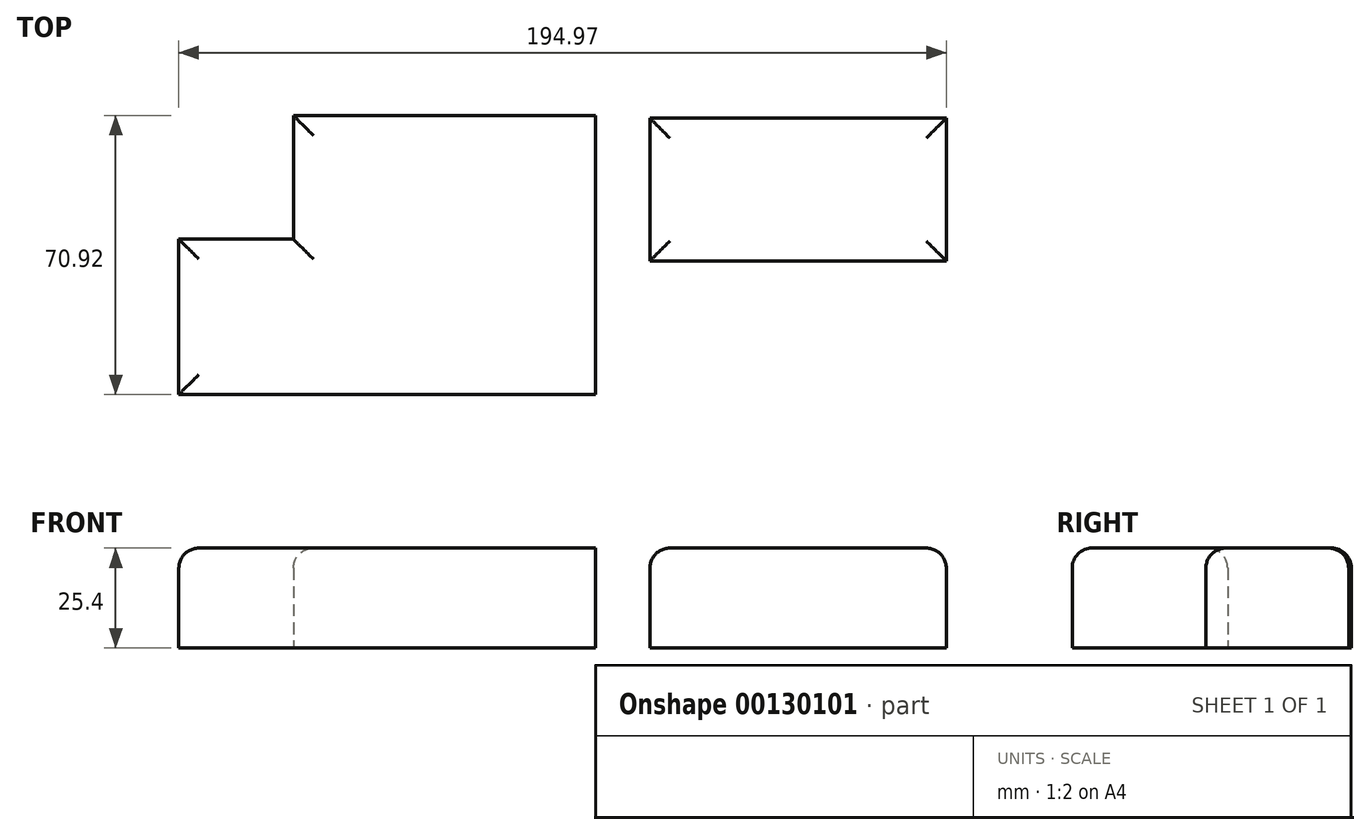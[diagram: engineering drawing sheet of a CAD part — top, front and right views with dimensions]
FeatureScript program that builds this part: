
annotation { "Feature Type Name" : "Feature", "Feature Type Description" : "" }
export const myFeature = defineFeature(function(context is Context, id is Id, definition is map)
    precondition{}
    {
        {
            var Q0;
            Q0=qCreatedBy(makeId("Top.planeOp"),FACE);
            var sketch = newSketch(context, id + "F0", { "sketchPlane" : qUnion([Q0])});
            skLineSegment(sketch, "E0.bottom", {"start": v(-80.87, 52.59) * mm, "end": v(-4.17, 52.59) * mm});
            skLineSegment(sketch, "E0.top", {"start": v(-80.87, -18.33) * mm, "end": v(-4.17, -18.33) * mm});
            skLineSegment(sketch, "E0.left", {"start": v(-80.87, 52.59) * mm, "end": v(-80.87, -18.33) * mm});
            skLineSegment(sketch, "E0.right", {"start": v(-4.17, 52.59) * mm, "end": v(-4.17, -18.33) * mm});
            skLineSegment(sketch, "E1.bottom", {"start": v(-45.3, -18.33) * mm, "end": v(-109.98, -18.33) * mm});
            skLineSegment(sketch, "E1.top", {"start": v(-45.3, 21.17) * mm, "end": v(-109.98, 21.17) * mm});
            skLineSegment(sketch, "E1.left", {"start": v(-45.3, -18.33) * mm, "end": v(-45.3, 21.17) * mm});
            skLineSegment(sketch, "E1.right", {"start": v(-109.98, -18.33) * mm, "end": v(-109.98, 21.17) * mm});
            skLineSegment(sketch, "E2.bottom", {"start": v(9.69, 51.9) * mm, "end": v(85, 51.9) * mm});
            skLineSegment(sketch, "E2.top", {"start": v(9.69, 15.62) * mm, "end": v(85, 15.62) * mm});
            skLineSegment(sketch, "E2.left", {"start": v(9.69, 51.9) * mm, "end": v(9.69, 15.62) * mm});
            skLineSegment(sketch, "E2.right", {"start": v(85, 51.9) * mm, "end": v(85, 15.62) * mm});
            skSolve(sketch);
        }
        {
            var Q0;
            Q0 = qSketchRegion(id + "F0", true);
            extrude(context, id + "F1", {"entities" : qUnion([Q0]), "depth" : 25.4 * mm});
        }
        {
            var Q0;
            Q0=makeQuery(id+"F1.opExtrude","CAP_EDGE",EDGE,{"disambiguationData":[OSD([sQuery(id+"F0.wireOp",EDGE,"E0.left")])],"isStart":false});
            var Q1;
            Q1=makeQuery(id+"F1.opExtrude","CAP_EDGE",EDGE,{"disambiguationData":[OSD([sQuery(id+"F0.wireOp",EDGE,"E0.bottom")])],"isStart":false});
            var Q2;
            Q2=makeQuery(id+"F1.opExtrude","CAP_EDGE",EDGE,{"disambiguationData":[OSD([sQuery(id+"F0.wireOp",EDGE,"E1.top")])],"isStart":false});
            var Q3;
            Q3=makeQuery(id+"F1.opExtrude","CAP_EDGE",EDGE,{"disambiguationData":[OSD([sQuery(id+"F0.wireOp",EDGE,"E1.right")])],"isStart":false});
            var Q4;
            Q4=makeQuery(id+"F1.opExtrude","CAP_EDGE",EDGE,{"disambiguationData":[OSD([sQuery(id+"F0.wireOp",EDGE,"E0.top"),sQuery(id+"F0.wireOp",EDGE,"E1.bottom")])],"isStart":false});
            var Q5;
            Q5=makeQuery(id+"F1.opExtrude","CAP_FACE",FACE,{"disambiguationData":[OSD([sQuery(id+"F0.wireOp",EDGE,"E2.bottom"),sQuery(id+"F0.wireOp",EDGE,"E2.top"),sQuery(id+"F0.wireOp",EDGE,"E2.left"),sQuery(id+"F0.wireOp",EDGE,"E2.right")])],"isStart":false});
            fillet(context, id + "F2", {"entities" : qUnion([Q0, Q1, Q2, Q3, Q4, Q5]), "radius" : 5.08 * mm, "tangentPropagation" : true, "allowEdgeOverflow" : false});
        }
    });
